# Revit family: ADB Gas Grills cupboard 410
name_source: partatom
category: Equipement spécialisé
units: mm (PartAtom-declared; Revit-internal decimal feet)

## family parameters
Basée sur le plan de construction = Non
Conserver l'orientation des annotations = Non
Cote de connecteur circulaire = Utiliser le diamètre
Couper avec des vides une fois chargée = Non
Numéro OmniClass = 23.40.40.14.17.11
Partagée = Non
Repère de localisation dans la pièce = Non
Titre OmniClass = Cookers, Ovens, Stoves
Toujours verticalement = Oui
Type d'élément = Normal

## types (5) — shared parameters
C = 200 mm  [stored 0.656168 ft]
Commentaires du type = Ambassade range - Gas grills & plancha
D = 725 mm  [stored 2.37861 ft]
E = 355 mm
F = 810 mm
Fabricant = Société Industrielle de Lacanche
Gas Size = 20.96 mm
Gas power kW = 6
URL = https://www.ambassade-de-bourgogne.com
URL Cutsheet = https://www.ambassade-de-bourgogne.com
zero-valued in all types: Elévation par défaut

## per-type parameters (varying)
| type | Bac | CKG | Description | GR_GL | Poids base | Position bouton | Position interrupteur | SLK_SLKC | Table |
| CMG 410 GR | Oui | Non | Ridged cast iron gas grill cupboard | Oui | 68.00 kg | 97 mm | 790 mm | Non | CME_CMG 410 GR_GL : GR |
| CMG 410 GL | Oui | Non | Smooth cast iron gasgrill cupboard | Oui | 68.00 kg | 97 mm | 790 mm | Non | CME_CMG 410 GR_GL : GL |
| CMG 410 SLK | Oui | Non | Smooth steel gas grill cupboard | Non | 68.00 kg | 97 mm | 790 mm | Oui | CME_CMG 410 SLK_SLKC : SLK |
| CMG 410 SLKC | Oui | Non | Smooth chrome gas grill cupboard | Non | 68.00 kg | 97 mm | 790 mm | Oui | CME_CMG 410 SLK_SLKC : SLKC |
| CMG 410 CKG | Non | Oui | Lava stones gas grill cupboard | Non | 64.00 kg | 110 mm  [stored 0.360892 ft] | 805 mm | Non | CMG410 CKG_gril gaz : CKG |

note: column(s) folded — value = type name in every type: Modèle

note: [stored X ft] marks values corroborated as IEEE doubles in the binary element streams (Revit-internal decimal feet)
